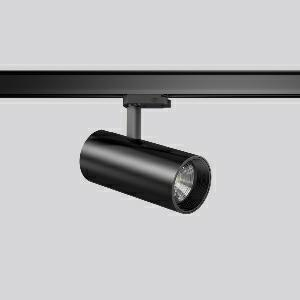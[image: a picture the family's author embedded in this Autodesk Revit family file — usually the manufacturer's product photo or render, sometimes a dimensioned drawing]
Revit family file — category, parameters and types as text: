
# Revit family: deecos_s_mini_742207_003_1_76_ad9d
name_source: partatom
category: Lighting Fixtures
units: mm (PartAtom-declared; Revit-internal decimal feet)

## family parameters
Cut with Voids When Loaded = No
Host = Face
Light Source = No
Part Type = Normal
Room Calculation Point = No
Round Connector Dimension = Use Diameter
Shared = No

## types (1)
- DEECOS S mini (1 x LED Modul 940, 3200 lm, 4000)
    Apparent Load = 29 VA
    Approval mark = CE
    CIE Flux Codes = 96 100 100 100 100
    Color Rendering = 92
    Color Temperature = 4000
    Default Elevation = 1800 mm
    Description = Series: DEECOS S mini
LED surface-mounted projector in modern design with no visible cooling ribs. Housing: die-cast aluminium, powder-coated. Rotation range: 356°. Swivel range: 90°. Black plastic ring and recessed LED to prevent glare from the side. Optical assembly with lens made of plastic (polycarbonate) for the best homogeneous light distribution - can be changed without tools. Best colour rendering index Ra>90. With adapter for RZB 3-circuit DALI tracks. Suitable for Track on ceiling, Wall track. High quality converter without flickering and stroboscopic effect. The following accessories can be mounted without use of tools: interchangeable lenses, decorative glasses, honeycomb louvre, clear and frosted diffusers, white interchangeable plastic ring. 
Colour: deep black, matt (RAL 9005)
Diameter: 87 mm
Height: 214 mm
Lamp: LED
Socket: without socket
Colour temperature: 4000K
Colour rendering index (CRI): 92
System power: 29 W
Rated luminous flux: 3200 lm
Luminous efficiency: 110 lm/W
Control gear: Converter, dimmable, DALI
Protection class: I
Type of protection: IP 20
    Height = 214 mm
    Lamp = 1 x LED Modul 940
    Lamp Light Flux = 3200 lm
    Lamp count = 1
    Length = 87 mm
    Lifetime = 50000 h
    Luminous efficacy = 110 lm/W
    Manufacturer = RZB
    ModVariant = No
    Model = 742207.003.1.76
    Mounting Place = Ceiling
    Mounting Type = Rail mounted
    Number of Poles = 1
    OnlyDefault = Yes
    Power Factor = 1
    Product Name = DEECOS S mini
    Product group = Track mounted projectors
    ProductGroupID = 301
    Protection Class = Protection class I
    Protection Degree = IP 20
    RLX_Detail_Level = 1
    RLX_Emergency_Light_Flux = 0 lm
    RLX_Emergency_Type = 0
    RLX_Emergency_Type_DB = No
    RlxData = <blob elided: 39157 chars, md5=3b3bac58>
    Socket = socket
    Standby Power = 0 W
    System Light Flux = 3200 lm
    System Power = 29 W
    Type Comments = Product without accessories
    Type Image = 741930.003.jpg
    URL = http://relux.com
    VarID = ---
    Voltage = 230 V
    Voltage Range = 220-240 V
    Weight = 0.00 kg
    Width = 0 mm  [stored 0 ft]

note: [stored X ft] marks values corroborated as IEEE doubles in the binary element streams (Revit-internal decimal feet)

## geometry (parser evidence)
native form markers: Blend x4, Sweep x12
no freeform markers — native parametric forms only
